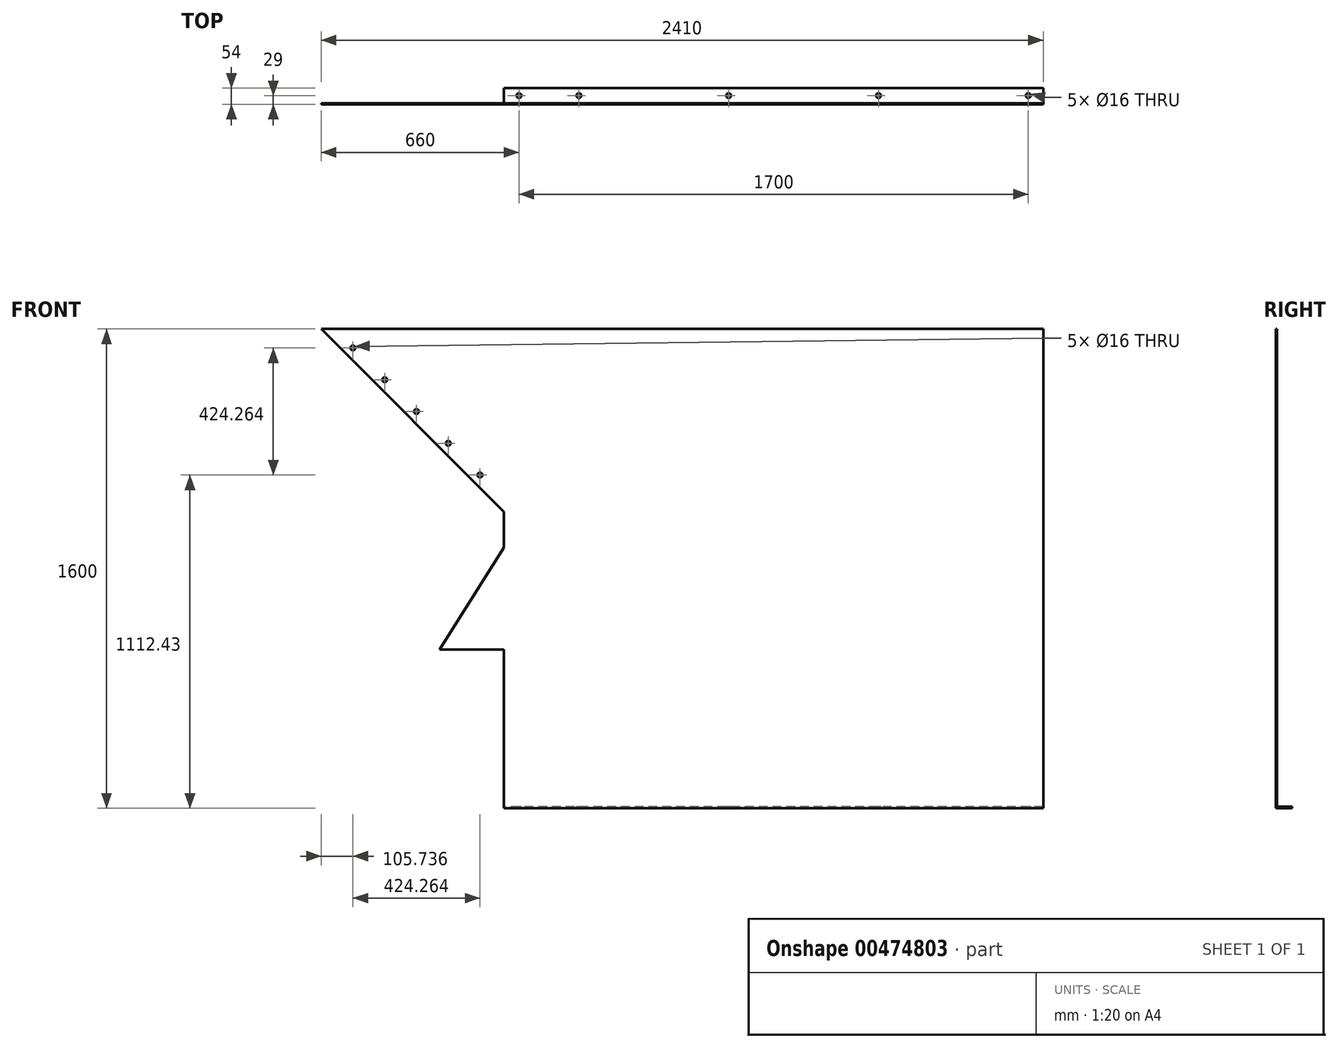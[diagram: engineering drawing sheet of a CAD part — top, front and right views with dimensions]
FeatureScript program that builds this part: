
annotation { "Feature Type Name" : "Feature", "Feature Type Description" : "" }
export const myFeature = defineFeature(function(context is Context, id is Id, definition is map)
    precondition{}
    {
        {
            var Q0;
            Q0=qCreatedBy(makeId("Front.planeOp"),FACE);
            var sketch = newSketch(context, id + "F0", { "sketchPlane" : qUnion([Q0])});
            skLineSegment(sketch, "E0", {"start": v(0, 0) * mm, "end": v(-1800, 0) * mm});
            skLineSegment(sketch, "E1", {"start": v(-1800, 0) * mm, "end": v(-1800, 530) * mm});
            skLineSegment(sketch, "E2", {"start": v(-1800, 530) * mm, "end": v(-2015, 530) * mm});
            skLineSegment(sketch, "E3", {"start": v(-1800, 0) * mm, "end": v(-1800, 870) * mm, "construction": true});
            skLineSegment(sketch, "E4", {"start": v(-2015, 530) * mm, "end": v(-1800, 870) * mm});
            skLineSegment(sketch, "E5", {"start": v(-1800, 870) * mm, "end": v(-1800, 990) * mm});
            skLineSegment(sketch, "E6", {"start": v(0, 0) * mm, "end": v(0, 1600) * mm});
            skLineSegment(sketch, "E7", {"start": v(0, 1600) * mm, "end": v(-2410, 1600) * mm});
            skLineSegment(sketch, "E8", {"start": v(-1800, 990) * mm, "end": v(-2410, 1600) * mm});
            skPoint(sketch, "E9", {"position": v(-2410, 1600) * mm});
            skCircle(sketch, "E10", {"center": v(-2198.2, 1430.62) * mm, "radius": 8 * mm});
            skLineSegment(sketch, "E11", {"start": v(-1731.8, 964.24) * mm, "end": v(-2341.8, 1574.24) * mm, "construction": true});
            skCircle(sketch, "E12", {"center": v(-2092.13, 1324.56) * mm, "radius": 8 * mm});
            skCircle(sketch, "E13", {"center": v(-1986.07, 1218.5) * mm, "radius": 8 * mm});
            skCircle(sketch, "E14", {"center": v(-1880, 1112.43) * mm, "radius": 8 * mm});
            skCircle(sketch, "E15", {"center": v(-2304.26, 1536.7) * mm, "radius": 8 * mm});
            skSolve(sketch);
        }
        {
            var Q0;
            Q0 = qSketchRegion(id + "F0", true);
            extrude(context, id + "F1", {"entities" : qUnion([Q0]), "depth" : 4 * mm});
        }
        {
            var Q0;
            Q0=makeQuery(id+"F1.opExtrude","CAP_FACE",FACE,{"disambiguationData":[OSD([sQuery(id+"F0.wireOp",EDGE,"E0"),sQuery(id+"F0.wireOp",EDGE,"E1"),sQuery(id+"F0.wireOp",EDGE,"E2"),sQuery(id+"F0.wireOp",EDGE,"E4"),sQuery(id+"F0.wireOp",EDGE,"E5"),sQuery(id+"F0.wireOp",EDGE,"E6"),sQuery(id+"F0.wireOp",EDGE,"E7"),sQuery(id+"F0.wireOp",EDGE,"E8"),sQuery(id+"F0.wireOp",EDGE,"E10"),sQuery(id+"F0.wireOp",EDGE,"E12"),sQuery(id+"F0.wireOp",EDGE,"E13"),sQuery(id+"F0.wireOp",EDGE,"E14"),sQuery(id+"F0.wireOp",EDGE,"E15")])],"isStart":true});
            var sketch = newSketch(context, id + "F2", { "sketchPlane" : qUnion([Q0])});
            skLineSegment(sketch, "E16.bottom", {"start": v(0, 0) * mm, "end": v(1800, 0) * mm});
            skLineSegment(sketch, "E16.top", {"start": v(0, 5) * mm, "end": v(1800, 5) * mm});
            skLineSegment(sketch, "E16.left", {"start": v(0, 0) * mm, "end": v(0, 5) * mm});
            skLineSegment(sketch, "E16.right", {"start": v(1800, 0) * mm, "end": v(1800, 5) * mm});
            skSolve(sketch);
        }
        {
            var Q0;
            Q0=makeQuery(id+"F2.imprint","IMPRINT",FACE,{"disambiguationData":[TD([[makeQuery(id+"F2.imprint","IMPRINT",EDGE,{"derivedFrom":sQuery(id+"F2.wireOp",EDGE,"E16.bottom")}),1.0]])]});
            extrude(context, id + "F3", {"entities" : qUnion([Q0]), "operationType" : NewBodyOperationType.ADD, "depth" : 50 * mm});
        }
        {
            var Q0;
            Q0=makeQuery(id+"F3.opExtrude","SWEPT_FACE",FACE,{"disambiguationData":[OSD([sQuery(id+"F2.wireOp",EDGE,"E16.top")])]});
            var sketch = newSketch(context, id + "F4", { "sketchPlane" : qUnion([Q0])});
            skLineSegment(sketch, "E17", {"start": v(0, 25) * mm, "end": v(-1800, 25) * mm, "construction": true});
            skCircle(sketch, "E18", {"center": v(-50, 25) * mm, "radius": 8 * mm});
            skCircle(sketch, "E19", {"center": v(-550, 25) * mm, "radius": 8 * mm});
            skCircle(sketch, "E20", {"center": v(-1050, 25) * mm, "radius": 8 * mm});
            skCircle(sketch, "E21", {"center": v(-1550, 25) * mm, "radius": 8 * mm});
            skCircle(sketch, "E22", {"center": v(-1750, 25) * mm, "radius": 8 * mm});
            skSolve(sketch);
        }
        {
            var Q0;
            Q0=makeQuery(id+"F4.imprint","IMPRINT",FACE,{"disambiguationData":[TD([[makeQuery(id+"F4.imprint","IMPRINT",EDGE,{"derivedFrom":sQuery(id+"F4.wireOp",EDGE,"E18")}),1.0]])]});
            var Q1;
            Q1=makeQuery(id+"F4.imprint","IMPRINT",FACE,{"disambiguationData":[TD([[makeQuery(id+"F4.imprint","IMPRINT",EDGE,{"derivedFrom":sQuery(id+"F4.wireOp",EDGE,"E19")}),1.0]])]});
            var Q2;
            Q2=makeQuery(id+"F4.imprint","IMPRINT",FACE,{"disambiguationData":[TD([[makeQuery(id+"F4.imprint","IMPRINT",EDGE,{"derivedFrom":sQuery(id+"F4.wireOp",EDGE,"E20")}),1.0]])]});
            var Q3;
            Q3=makeQuery(id+"F4.imprint","IMPRINT",FACE,{"disambiguationData":[TD([[makeQuery(id+"F4.imprint","IMPRINT",EDGE,{"derivedFrom":sQuery(id+"F4.wireOp",EDGE,"E21")}),1.0]])]});
            var Q4;
            Q4=makeQuery(id+"F4.imprint","IMPRINT",FACE,{"disambiguationData":[TD([[makeQuery(id+"F4.imprint","IMPRINT",EDGE,{"derivedFrom":sQuery(id+"F4.wireOp",EDGE,"E22")}),1.0]])]});
            var Q5;
            Q5=sQuery(id+"F4.wireOp",EDGE,"E18");
            extrude(context, id + "F5", {"entities" : qUnion([Q0, Q1, Q2, Q3, Q4]), "operationType" : NewBodyOperationType.REMOVE, "surfaceEntities" : qUnion([Q5]), "oppositeDirection" : true, "depth" : 25 * mm});
        }
    });
